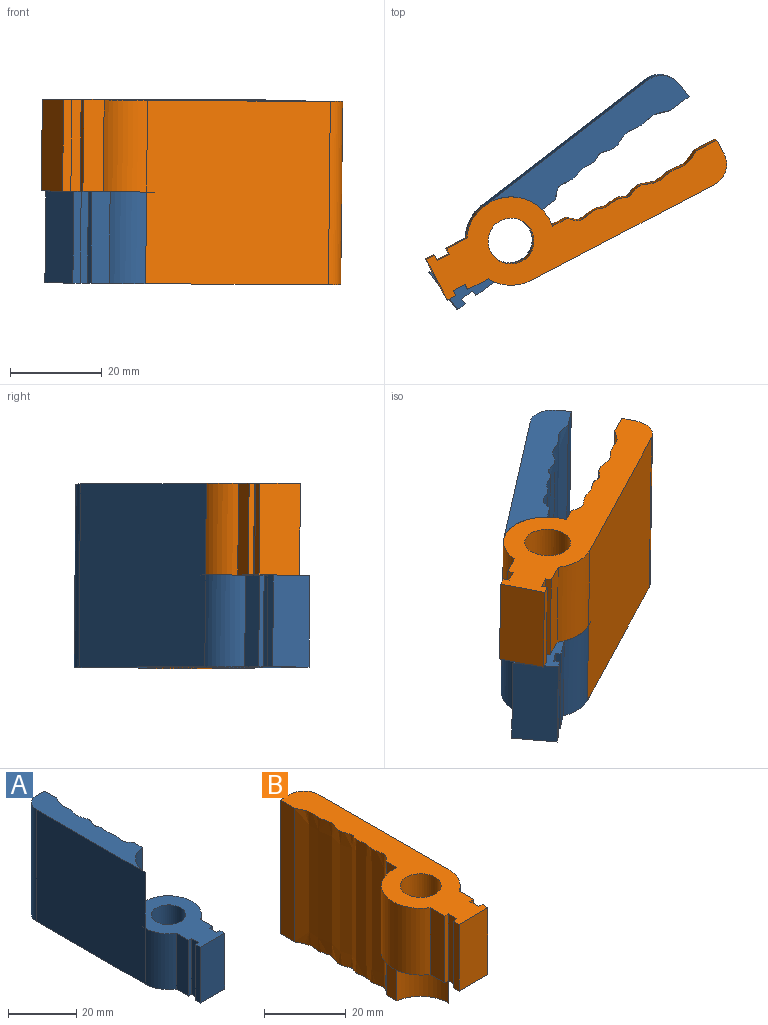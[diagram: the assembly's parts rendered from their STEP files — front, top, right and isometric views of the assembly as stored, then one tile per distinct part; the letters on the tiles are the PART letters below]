
ASSEMBLY  parts=2 mates=1
PART A: 24 faces, bbox 19.3x68.2x40 mm
  f0: plane 45x40mm, normal (-1,0,0), area 1800mm2, adj f1,f6,f7,f8,f9
  f1: cylinder r=9.64mm len=20mm, axis (0,0,-1), area 276.9mm2, adj f0,f2,f7,f23
  f2: plane 40x3.64mm, normal (1,0,0), area 145.5mm2, adj f1,f3,f7,f8,f10
  f3: extruded ~40x31.81mm, area 1331.7mm2, adj f2,f4,f7,f8
  f4: plane 40x5mm, normal (1,0,0), area 200mm2, adj f3,f5,f7,f8
  f5: plane 40x3.35mm, normal (0,1,0), area 133.9mm2, adj f4,f6,f7,f8
  f6: cylinder r=5mm len=40mm, axis (0,0,-1), area 314.2mm2, adj f0,f5,f7,f8
  f7: plane 50x8.35mm, normal (0,0,1), area 305.8mm2, adj f0,f1,f2,f3,f4,f5,f6
  f8: plane 68.24x19.28mm, normal (0,0,-1), area 602.2mm2, adj f0,f2,f3,f4,f5,f6,f9,f10
  f9: cylinder r=9.64mm len=20mm, axis (0,0,-1), area 197.8mm2, adj f0,f8,f11,f23
  f10: cylinder r=9.64mm len=20mm, axis (0,0,-1), area 526.7mm2, adj f2,f8,f22,f23
  f11: plane 20x5mm, normal (-1,0,0), area 100mm2, adj f8,f9,f12,f23
  f12: plane 20x1.29mm, normal (0,-1,0), area 25.8mm2, adj f8,f11,f13,f23
  f13: plane 20x2.97mm, normal (-1,0,0), area 59.4mm2, adj f8,f12,f14,f23
  f14: plane 20x1.29mm, normal (0,1,0), area 25.8mm2, adj f8,f13,f15,f23
  f15: plane 20x2.03mm, normal (-1,0,0), area 40.6mm2, adj f8,f14,f16,f23
  f16: plane 20x10mm, normal (0,-1,0), area 200mm2, adj f8,f15,f17,f23
  f17: plane 20x2.03mm, normal (1,0,0), area 40.6mm2, adj f8,f16,f18,f23
  f18: plane 20x1.29mm, normal (0,1,0), area 25.8mm2, adj f8,f17,f19,f23
  f19: plane 20x2.97mm, normal (1,0,0), area 59.4mm2, adj f8,f18,f20,f23
  f20: plane 20x1.29mm, normal (0,-1,0), area 25.8mm2, adj f8,f19,f22,f23
  f21: cylinder r=5mm len=20mm, axis (0,0,-1), area 628.3mm2, adj f8,f23
  f22: plane 20x5mm, normal (1,0,0), area 100mm2, adj f8,f10,f20,f23
  f23: plane 27.89x19.28mm, normal (0,0,1), area 296.4mm2, adj f1,f9,f10,f11,f12,f13,f14,f15
PART B: 24 faces, bbox 19.3x68.2x40 mm
  f0: cylinder r=9.64mm len=20mm, axis (0,0,-1), area 276.9mm2, adj f1,f6,f8,f23
  f1: plane 45x40mm, normal (1,0,0), area 1800mm2, adj f0,f2,f7,f8,f9
  f2: cylinder r=5mm len=40mm, axis (0,0,-1), area 314.2mm2, adj f1,f3,f7,f8
  f3: plane 40x3.35mm, normal (0,1,0), area 133.9mm2, adj f2,f4,f7,f8
  f4: plane 40x5mm, normal (-1,0,0), area 200mm2, adj f3,f5,f7,f8
  f5: extruded ~40x31.81mm, area 1331.7mm2, adj f4,f6,f7,f8
  f6: plane 40x3.64mm, normal (-1,0,0), area 145.5mm2, adj f0,f5,f7,f8,f10
  f7: plane 68.24x19.28mm, normal (0,0,1), area 602.2mm2, adj f1,f2,f3,f4,f5,f6,f9,f10
  f8: plane 50x8.35mm, normal (0,0,-1), area 305.8mm2, adj f0,f1,f2,f3,f4,f5,f6
  f9: cylinder r=9.64mm len=20mm, axis (0,0,-1), area 197.8mm2, adj f1,f7,f21,f23
  f10: cylinder r=9.64mm len=20mm, axis (0,0,-1), area 526.7mm2, adj f6,f7,f11,f23
  f11: plane 20x5mm, normal (-1,0,0), area 100mm2, adj f7,f10,f12,f23
  f12: plane 20x1.29mm, normal (0,-1,0), area 25.8mm2, adj f7,f11,f13,f23
  f13: plane 20x2.97mm, normal (-1,0,0), area 59.4mm2, adj f7,f12,f14,f23
  f14: plane 20x1.29mm, normal (0,1,0), area 25.8mm2, adj f7,f13,f15,f23
  f15: plane 20x2.03mm, normal (-1,0,0), area 40.6mm2, adj f7,f14,f16,f23
  f16: plane 20x10mm, normal (0,-1,0), area 200mm2, adj f7,f15,f17,f23
  f17: plane 20x2.03mm, normal (1,0,0), area 40.6mm2, adj f7,f16,f18,f23
  f18: plane 20x1.29mm, normal (0,1,0), area 25.8mm2, adj f7,f17,f19,f23
  f19: plane 20x2.97mm, normal (1,0,0), area 59.4mm2, adj f7,f18,f20,f23
  f20: plane 20x1.29mm, normal (0,-1,0), area 25.8mm2, adj f7,f19,f21,f23
  f21: plane 20x5mm, normal (1,0,0), area 100mm2, adj f7,f9,f20,f23
  f22: cylinder r=5mm len=20mm, axis (0,0,-1), area 628.3mm2, adj f7,f23
  f23: plane 27.89x19.28mm, normal (0,0,-1), area 296.4mm2, adj f0,f9,f10,f11,f12,f13,f14,f15
PLACE A rot(axis=(0,0.01,-1),52.4deg) t=(-40.19,-91.21,3.58)mm
PLACE B rot(axis=(0,0.01,-1),62.4deg) t=(-88.84,-14.94,24.7)mm fixed
MATE revolute A.f1 <-> B.f0  axis (0.01,-0.01,1) through (-67.75,-55.29,24.16)mm
